# Revit family: MixerSet_Hob_Abey_PocoP_Sink_SingleSprayHead_FaceBased
name_source: partatom
category: Plumbing Fixtures
units: mm (PartAtom-declared; Revit-internal decimal feet)

## family parameters
Cut with Voids When Loaded = No
Host = Face
Maintain Annotation Orientation = No
OmniClass Number = 23.31.11.19
OmniClass Title = Faucet Mixing Valves
Part Type = Normal
Room Calculation Point = No
Round Connector Dimension = Use Diameter
Shared = No

## types (3) — shared parameters
Assembly Code = C1030210
CW Connection = Yes
Default Elevation = 0 mm
Description = Poco P Pull Out Goose Neck Hob Set 368mm
HW Connection = Yes
IfcExportAs = ifcValve
IfcExportType = FAUCET
Manufacturer = Abey
ManufacturerOverallDepth = 257.5 mm
ManufacturerOverallHeight = 367.5 mm
ManufacturerOverallWidth = 180 mm
ManufacturerURLProductSpecific = https://www.abeyspecifier.com.au
ModifiedIssue = 20251103 $
URL = https://www.abey.com.au
Uniclass2015Code = Pr_40_20_87_55
Uniclass2015Title = Mixer taps
Uniclass2015Version = Products v1.38
Vent Connection = No
Waste Connection = No
zero-valued in all types: Cost

## per-type parameters (varying)
| type | BodyMaterial | ManufacturerSpecCode | Model | Type Comments |
| Gun Metal (8K2-GM-LF) | Metal_Abey_GunMetal | 8K2-GM-LF | 8K2-GM-LF | Mixer Set - Hob - Gun Metal |
| Brushed Brass (8K2-BB-LF) | Metal_Abey_Brass | 8K2-BB-LF | 8K2-BB-LF | Mixer Set - Hob - Brushed Brass |
| Brushed Nickel (8K2-BN-LF) | Metal_Abey_BrushedNickel | 8K2-BN-LF | 8K2-BN-LF | Mixer Set - Hob - Brushed Nickel |

## geometry (parser evidence)
native form markers: Sweep x4
no freeform markers — native parametric forms only
